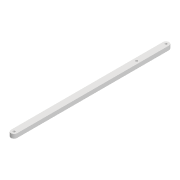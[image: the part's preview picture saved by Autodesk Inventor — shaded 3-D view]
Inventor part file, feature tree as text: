
AUTODESK INVENTOR PART (.ipt)
format: ipt  version: 2022 (Build 260153000, 153)  size: 93,184 bytes
history: native  units: mm
features: extrude x1, sketch x1
ambient origin geometry x8: Origin, YZ Plane, XZ Plane, XY Plane, X Axis, Y Axis, Z Axis, Center Point
bodies: Solid1 (feature_tree)
feature tree (2):
  extrude  "Extrusion1"  Depth=120.259mm
  sketch  "Sketch1"  dims[d0=2.2mm d1=2.2mm d2=6.0mm d3=149.325mm d6=4.0mm d7=0.0mm d14=2.2mm d15=120.259mm]
